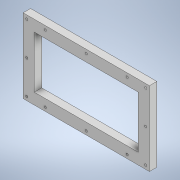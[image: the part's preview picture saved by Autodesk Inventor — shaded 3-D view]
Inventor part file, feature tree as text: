
AUTODESK INVENTOR PART (.ipt)
format: ipt  version: 2022.2 (Build 262287030, 287C)  size: 159,232 bytes
history: native  units: in
note: dims shown in document units (in); Inventor stores cm internally (conversion verified against a paired STEP export)
features: sketch x3, extrude x2, hole x2
ambient origin geometry x8: Origin, YZ Plane, XZ Plane, XY Plane, X Axis, Y Axis, Z Axis, Center Point
bodies: Solid1 (feature_tree)
feature tree (7):
  extrude  "Extrusion1"  Depth=3.937in
  extrude  "Extrusion2"  Depth=5.5118in
  hole  "Hole1"  [1 undecoded]
  hole  "Hole2"  [1 undecoded]
  sketch  "Sketch1"  dims[d0=6.6929in d1=3.937in]
  sketch  "Sketch2"  dims[d2=0.3937in d3=0.0in d4=5.5118in]
  sketch  "Sketch4"  dims[d5=2.7559in d6=0.3937in d7=0.0in d38=0.125in d39=0.2953in d40=0.1476in d41=0.0984in d42=90.0deg d43=0.1969in d44=0.0in d45=0.1969in d53=0.7874in d55=1.9685in d56=0.3937in d58=0.3937in d60=0.7874in d62=6.2992in d63=0.3937in d65=0.3937in d72=1.9685in d73=0.1969in d74=0.1969in d75=3.3465in d78=0.9843in d80=0.1969in d81=0.1969in d82=0.9843in d83=0.7874in d85=6.2992in d86=0.3937in d88=0.3937in d106=0.1181in d107=0.2953in d108=0.1476in d109=0.0984in d110=90.0deg d111=0.1969in d112=0.0in d115=0.1969in d116=0.1969in d117=0.1969in d118=0.7874in d120=3.5433in d121=0.3937in d123=0.3937in d125=1.7717in d131=0.9843in d156=2.2638in d157=0.7874in d159=2.1654in d160=0.7874in d162=3.5433in d158=0.3937in d161=0.1476in d163=0.2953in d164=0.8108in d165=0.0246in d166=0.2953in d167=0.1476in]
note: 2 required parameter values undecoded (feature->parameter linkage not recoverable at this tier; creation-order binding heuristic only, values carry confidence <= 0.55)
